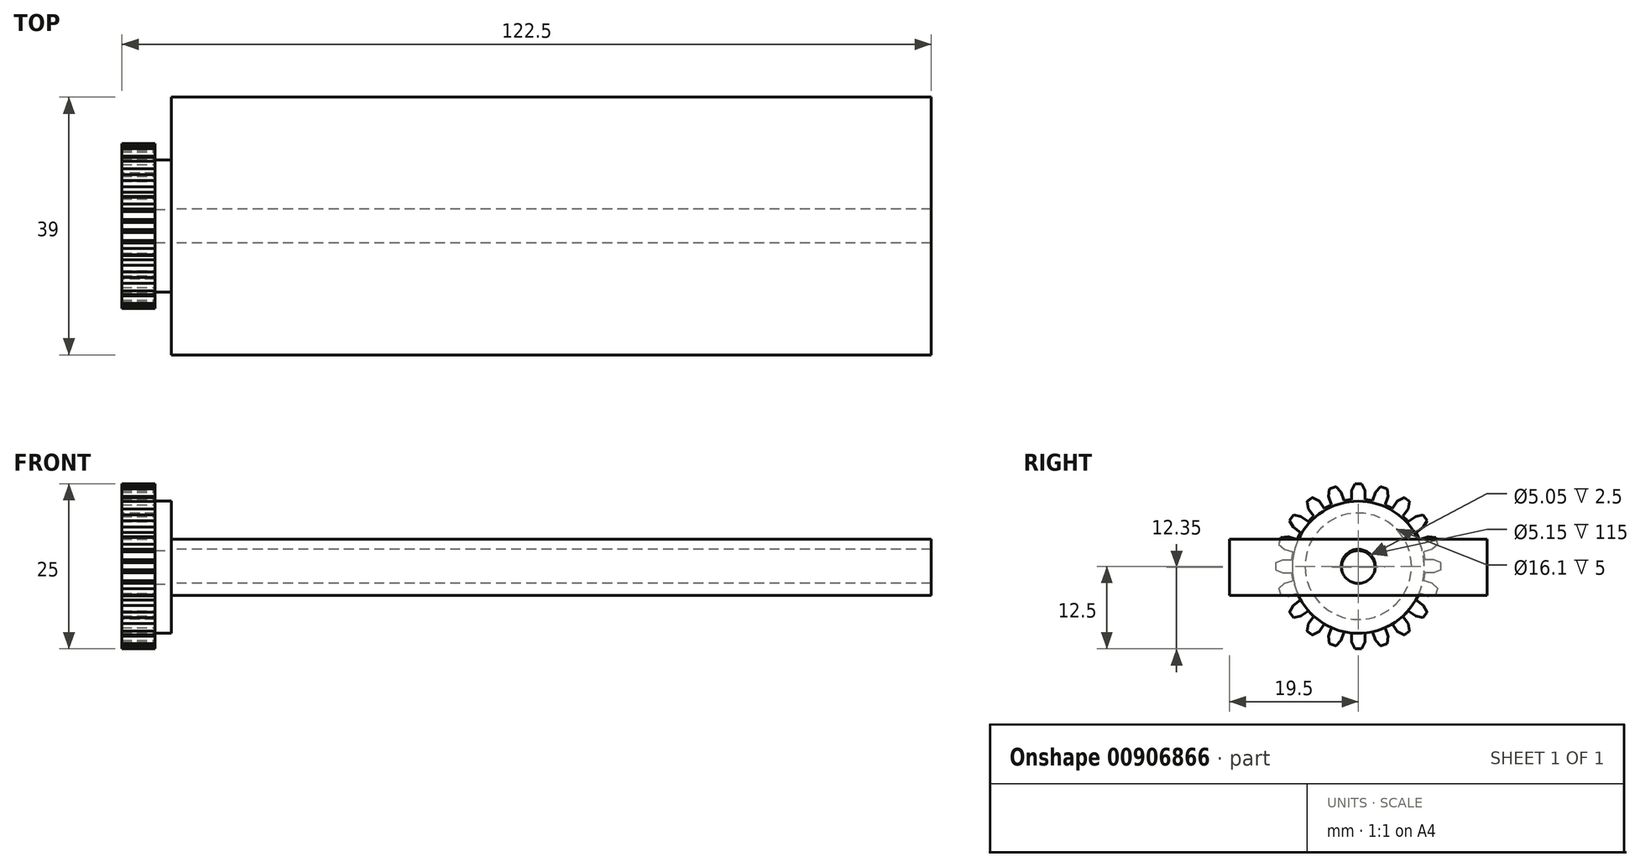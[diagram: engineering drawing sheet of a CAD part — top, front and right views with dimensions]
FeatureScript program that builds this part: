
annotation { "Feature Type Name" : "Feature", "Feature Type Description" : "" }
export const myFeature = defineFeature(function(context is Context, id is Id, definition is map)
    precondition{}
    {
        {
            var Q0;
            Q0=qCreatedBy(makeId("Top.planeOp"),FACE);
            var sketch = newSketch(context, id + "F0", { "sketchPlane" : qUnion([Q0])});
            skLineSegment(sketch, "E0.bottom", {"start": v(57.5, 19.5) * mm, "end": v(-57.5, 19.5) * mm});
            skLineSegment(sketch, "E0.top", {"start": v(57.5, -19.5) * mm, "end": v(-57.5, -19.5) * mm});
            skLineSegment(sketch, "E0.left", {"start": v(57.5, 19.5) * mm, "end": v(57.5, -19.5) * mm});
            skLineSegment(sketch, "E0.right", {"start": v(-57.5, 19.5) * mm, "end": v(-57.5, -19.5) * mm});
            skPoint(sketch, "E0.middle", {"position": v(0, 0) * mm});
            skSolve(sketch);
        }
        {
            var Q0;
            Q0 = qSketchRegion(id + "F0", true);
            extrude(context, id + "F1", {"entities" : qUnion([Q0]), "depth" : 8.5 * mm, "offsetDistance" : 25 * mm});
        }
        {
            var Q0;
            Q0=makeQuery(id+"F1.opExtrude","SWEPT_FACE",FACE,{"disambiguationData":[OSD([sQuery(id+"F0.wireOp",EDGE,"E0.right")])]});
            var sketch = newSketch(context, id + "F2", { "sketchPlane" : qUnion([Q0])});
            skLineSegment(sketch, "E1", {"start": v(-19.5, 4.25) * mm, "end": v(19.5, 4.25) * mm, "construction": true});
            skLineSegment(sketch, "E2", {"start": v(0, 8.5) * mm, "end": v(0, 0) * mm, "construction": true});
            skCircle(sketch, "E3", {"center": v(0, 4.25) * mm, "radius": 2.52 * mm});
            skCircle(sketch, "E4", {"center": v(0, 4.25) * mm, "radius": 10 * mm});
            skSolve(sketch);
        }
        {
            var Q0;
            Q0 = qSketchRegion(id + "F2", true);
            extrude(context, id + "F3", {"entities" : qUnion([Q0]), "operationType" : NewBodyOperationType.ADD, "depth" : 2.5 * mm, "offsetDistance" : 25 * mm});
        }
        {
            var Q0;
            {var subQ0=sQuery(id+"F0.wireOp",EDGE,"E0.right");var subQ1=makeQuery(id+"F1.opExtrude","SWEPT_FACE",FACE,{"disambiguationData":[OSD([subQ0])]});var subQ2=sQuery(id+"F0.wireOp",EDGE,"E0.top");Q0=makeQuery(id+"F3.boolean.opBoolean","SPLIT",FACE,{"disambiguationData":[TD([makeQuery(id+"F1.opExtrude","SWEPT_FACE",FACE,{"disambiguationData":[OSD([subQ2])]})])],"derivedFrom":subQ1});}
            var sketch = newSketch(context, id + "F4", { "sketchPlane" : qUnion([Q0])});
            skCircle(sketch, "E5.0", {"center": v(0, 4.4) * mm, "radius": 2.58 * mm});
            skSolve(sketch);
        }
        {
            var Q0;
            Q0 = qSketchRegion(id + "F4", true);
            extrude(context, id + "F5", {"entities" : qUnion([Q0]), "operationType" : NewBodyOperationType.REMOVE, "endBound" : BoundingType.THROUGH_ALL, "oppositeDirection" : true, "depth" : 90 * mm, "offsetDistance" : 25 * mm});
        }
        {
            var Q0;
            Q0=makeQuery(id+"F3.opExtrude","CAP_FACE",FACE,{"disambiguationData":[OSD([sQuery(id+"F2.wireOp",EDGE,"E3"),sQuery(id+"F2.wireOp",EDGE,"E4")])],"isStart":false});
            var sketch = newSketch(context, id + "F6", { "sketchPlane" : qUnion([Q0])});
            skCircle(sketch, "E6", {"center": v(0, 4.4) * mm, "radius": 11.5 * mm, "construction": true});
            skLineSegment(sketch, "E7", {"start": v(-0.52, 16.89) * mm, "end": v(-1, 15.86) * mm});
            skLineSegment(sketch, "E8", {"start": v(-1, 15.86) * mm, "end": v(-1, 14.5) * mm});
            skLineSegment(sketch, "E9", {"start": v(-0.52, 19.42) * mm, "end": v(-0.52, 14.1) * mm, "construction": true});
            skLineSegment(sketch, "E10.MirrorCS", {"start": v(0.52, 16.89) * mm, "end": v(1, 15.86) * mm});
            skLineSegment(sketch, "E11.MirrorCS", {"start": v(1, 15.86) * mm, "end": v(1, 14.5) * mm});
            skArc(sketch, "E12", {"start": v(-0.52, 16.89) * mm, "mid": v(0, 16.9) * mm, "end": v(0.52, 16.89) * mm});
            skLineSegment(sketch, "E13.1.0", {"start": v(-4.5, 14.99) * mm, "end": v(-4.07, 13.7) * mm});
            skLineSegment(sketch, "E13.1.1", {"start": v(-3.37, 16.44) * mm, "end": v(-2.59, 15.6) * mm});
            skLineSegment(sketch, "E13.1.2", {"start": v(-2.59, 15.6) * mm, "end": v(-2.17, 14.31) * mm});
            skLineSegment(sketch, "E13.1.3", {"start": v(-4.35, 16.12) * mm, "end": v(-4.5, 14.99) * mm});
            skArc(sketch, "E13.1.4", {"start": v(-4.35, 16.12) * mm, "mid": v(-3.86, 16.29) * mm, "end": v(-3.37, 16.44) * mm});
            skLineSegment(sketch, "E13.2.0", {"start": v(-7.54, 13.08) * mm, "end": v(-6.74, 11.98) * mm});
            skLineSegment(sketch, "E13.2.1", {"start": v(-6.92, 14.8) * mm, "end": v(-5.92, 14.26) * mm});
            skLineSegment(sketch, "E13.2.2", {"start": v(-5.92, 14.26) * mm, "end": v(-5.13, 13.16) * mm});
            skLineSegment(sketch, "E13.2.3", {"start": v(-7.76, 14.2) * mm, "end": v(-7.54, 13.08) * mm});
            skArc(sketch, "E13.2.4", {"start": v(-7.76, 14.2) * mm, "mid": v(-7.35, 14.51) * mm, "end": v(-6.92, 14.8) * mm});
            skLineSegment(sketch, "E13.3.0", {"start": v(-9.86, 10.32) * mm, "end": v(-8.76, 9.53) * mm});
            skLineSegment(sketch, "E13.3.1", {"start": v(-9.8, 12.16) * mm, "end": v(-8.68, 11.94) * mm});
            skLineSegment(sketch, "E13.3.2", {"start": v(-8.68, 11.94) * mm, "end": v(-7.58, 11.14) * mm});
            skLineSegment(sketch, "E13.3.3", {"start": v(-10.4, 11.32) * mm, "end": v(-9.86, 10.32) * mm});
            skArc(sketch, "E13.3.4", {"start": v(-10.4, 11.32) * mm, "mid": v(-10.11, 11.75) * mm, "end": v(-9.8, 12.16) * mm});
            skLineSegment(sketch, "E13.4.0", {"start": v(-11.2, 6.99) * mm, "end": v(-9.91, 6.57) * mm});
            skLineSegment(sketch, "E13.4.1", {"start": v(-11.72, 8.75) * mm, "end": v(-10.59, 8.9) * mm});
            skLineSegment(sketch, "E13.4.2", {"start": v(-10.59, 8.9) * mm, "end": v(-9.3, 8.47) * mm});
            skLineSegment(sketch, "E13.4.3", {"start": v(-12.04, 7.77) * mm, "end": v(-11.2, 6.99) * mm});
            skArc(sketch, "E13.4.4", {"start": v(-12.04, 7.77) * mm, "mid": v(-11.89, 8.26) * mm, "end": v(-11.72, 8.75) * mm});
            skLineSegment(sketch, "E13.5.0", {"start": v(-11.46, 3.4) * mm, "end": v(-10.1, 3.4) * mm});
            skLineSegment(sketch, "E13.5.1", {"start": v(-12.49, 4.92) * mm, "end": v(-11.46, 5.4) * mm});
            skLineSegment(sketch, "E13.5.2", {"start": v(-11.46, 5.4) * mm, "end": v(-10.1, 5.4) * mm});
            skLineSegment(sketch, "E13.5.3", {"start": v(-12.49, 3.88) * mm, "end": v(-11.46, 3.4) * mm});
            skArc(sketch, "E13.5.4", {"start": v(-12.49, 3.88) * mm, "mid": v(-12.5, 4.4) * mm, "end": v(-12.49, 4.92) * mm});
            skLineSegment(sketch, "E13.6.0", {"start": v(-10.59, -0.1) * mm, "end": v(-9.3, 0.33) * mm});
            skLineSegment(sketch, "E13.6.1", {"start": v(-12.04, 1.03) * mm, "end": v(-11.2, 1.81) * mm});
            skLineSegment(sketch, "E13.6.2", {"start": v(-11.2, 1.81) * mm, "end": v(-9.91, 2.23) * mm});
            skLineSegment(sketch, "E13.6.3", {"start": v(-11.72, 0.05) * mm, "end": v(-10.59, -0.1) * mm});
            skArc(sketch, "E13.6.4", {"start": v(-11.72, 0.05) * mm, "mid": v(-11.89, 0.54) * mm, "end": v(-12.04, 1.03) * mm});
            skLineSegment(sketch, "E13.7.0", {"start": v(-8.68, -3.14) * mm, "end": v(-7.58, -2.34) * mm});
            skLineSegment(sketch, "E13.7.1", {"start": v(-10.4, -2.52) * mm, "end": v(-9.86, -1.52) * mm});
            skLineSegment(sketch, "E13.7.2", {"start": v(-9.86, -1.52) * mm, "end": v(-8.76, -0.73) * mm});
            skLineSegment(sketch, "E13.7.3", {"start": v(-9.8, -3.36) * mm, "end": v(-8.68, -3.14) * mm});
            skArc(sketch, "E13.7.4", {"start": v(-9.8, -3.36) * mm, "mid": v(-10.11, -2.95) * mm, "end": v(-10.4, -2.52) * mm});
            skLineSegment(sketch, "E13.8.0", {"start": v(-5.92, -5.46) * mm, "end": v(-5.13, -4.36) * mm});
            skLineSegment(sketch, "E13.8.1", {"start": v(-7.76, -5.4) * mm, "end": v(-7.54, -4.28) * mm});
            skLineSegment(sketch, "E13.8.2", {"start": v(-7.54, -4.28) * mm, "end": v(-6.74, -3.18) * mm});
            skLineSegment(sketch, "E13.8.3", {"start": v(-6.92, -6) * mm, "end": v(-5.92, -5.46) * mm});
            skArc(sketch, "E13.8.4", {"start": v(-6.92, -6) * mm, "mid": v(-7.35, -5.71) * mm, "end": v(-7.76, -5.4) * mm});
            skLineSegment(sketch, "E13.9.0", {"start": v(-2.59, -6.8) * mm, "end": v(-2.17, -5.51) * mm});
            skLineSegment(sketch, "E13.9.1", {"start": v(-4.35, -7.32) * mm, "end": v(-4.5, -6.19) * mm});
            skLineSegment(sketch, "E13.9.2", {"start": v(-4.5, -6.19) * mm, "end": v(-4.07, -4.9) * mm});
            skLineSegment(sketch, "E13.9.3", {"start": v(-3.37, -7.64) * mm, "end": v(-2.59, -6.8) * mm});
            skArc(sketch, "E13.9.4", {"start": v(-3.37, -7.64) * mm, "mid": v(-3.86, -7.49) * mm, "end": v(-4.35, -7.32) * mm});
            skLineSegment(sketch, "E13.10.0", {"start": v(1, -7.06) * mm, "end": v(1, -5.7) * mm});
            skLineSegment(sketch, "E13.10.1", {"start": v(-0.52, -8.09) * mm, "end": v(-1, -7.06) * mm});
            skLineSegment(sketch, "E13.10.2", {"start": v(-1, -7.06) * mm, "end": v(-1, -5.7) * mm});
            skLineSegment(sketch, "E13.10.3", {"start": v(0.52, -8.09) * mm, "end": v(1, -7.06) * mm});
            skArc(sketch, "E13.10.4", {"start": v(0.52, -8.09) * mm, "mid": v(0, -8.1) * mm, "end": v(-0.52, -8.09) * mm});
            skLineSegment(sketch, "E13.11.0", {"start": v(4.5, -6.19) * mm, "end": v(4.07, -4.9) * mm});
            skLineSegment(sketch, "E13.11.1", {"start": v(3.37, -7.64) * mm, "end": v(2.59, -6.8) * mm});
            skLineSegment(sketch, "E13.11.2", {"start": v(2.59, -6.8) * mm, "end": v(2.17, -5.51) * mm});
            skLineSegment(sketch, "E13.11.3", {"start": v(4.35, -7.32) * mm, "end": v(4.5, -6.19) * mm});
            skArc(sketch, "E13.11.4", {"start": v(4.35, -7.32) * mm, "mid": v(3.86, -7.49) * mm, "end": v(3.37, -7.64) * mm});
            skLineSegment(sketch, "E13.12.0", {"start": v(7.54, -4.28) * mm, "end": v(6.74, -3.18) * mm});
            skLineSegment(sketch, "E13.12.1", {"start": v(6.92, -6) * mm, "end": v(5.92, -5.46) * mm});
            skLineSegment(sketch, "E13.12.2", {"start": v(5.92, -5.46) * mm, "end": v(5.13, -4.36) * mm});
            skLineSegment(sketch, "E13.12.3", {"start": v(7.76, -5.4) * mm, "end": v(7.54, -4.28) * mm});
            skArc(sketch, "E13.12.4", {"start": v(7.76, -5.4) * mm, "mid": v(7.35, -5.71) * mm, "end": v(6.92, -6) * mm});
            skLineSegment(sketch, "E13.13.0", {"start": v(9.86, -1.52) * mm, "end": v(8.76, -0.73) * mm});
            skLineSegment(sketch, "E13.13.1", {"start": v(9.8, -3.36) * mm, "end": v(8.68, -3.14) * mm});
            skLineSegment(sketch, "E13.13.2", {"start": v(8.68, -3.14) * mm, "end": v(7.58, -2.34) * mm});
            skLineSegment(sketch, "E13.13.3", {"start": v(10.4, -2.52) * mm, "end": v(9.86, -1.52) * mm});
            skArc(sketch, "E13.13.4", {"start": v(10.4, -2.52) * mm, "mid": v(10.11, -2.95) * mm, "end": v(9.8, -3.36) * mm});
            skLineSegment(sketch, "E13.14.0", {"start": v(11.2, 1.81) * mm, "end": v(9.91, 2.23) * mm});
            skLineSegment(sketch, "E13.14.1", {"start": v(11.72, 0.05) * mm, "end": v(10.59, -0.1) * mm});
            skLineSegment(sketch, "E13.14.2", {"start": v(10.59, -0.1) * mm, "end": v(9.3, 0.33) * mm});
            skLineSegment(sketch, "E13.14.3", {"start": v(12.04, 1.03) * mm, "end": v(11.2, 1.81) * mm});
            skArc(sketch, "E13.14.4", {"start": v(12.04, 1.03) * mm, "mid": v(11.89, 0.54) * mm, "end": v(11.72, 0.05) * mm});
            skLineSegment(sketch, "E13.15.0", {"start": v(11.46, 5.4) * mm, "end": v(10.1, 5.4) * mm});
            skLineSegment(sketch, "E13.15.1", {"start": v(12.49, 3.88) * mm, "end": v(11.46, 3.4) * mm});
            skLineSegment(sketch, "E13.15.2", {"start": v(11.46, 3.4) * mm, "end": v(10.1, 3.4) * mm});
            skLineSegment(sketch, "E13.15.3", {"start": v(12.49, 4.92) * mm, "end": v(11.46, 5.4) * mm});
            skArc(sketch, "E13.15.4", {"start": v(12.49, 4.92) * mm, "mid": v(12.5, 4.4) * mm, "end": v(12.49, 3.88) * mm});
            skLineSegment(sketch, "E13.16.0", {"start": v(10.59, 8.9) * mm, "end": v(9.3, 8.47) * mm});
            skLineSegment(sketch, "E13.16.1", {"start": v(12.04, 7.77) * mm, "end": v(11.2, 6.99) * mm});
            skLineSegment(sketch, "E13.16.2", {"start": v(11.2, 6.99) * mm, "end": v(9.91, 6.57) * mm});
            skLineSegment(sketch, "E13.16.3", {"start": v(11.72, 8.75) * mm, "end": v(10.59, 8.9) * mm});
            skArc(sketch, "E13.16.4", {"start": v(11.72, 8.75) * mm, "mid": v(11.89, 8.26) * mm, "end": v(12.04, 7.77) * mm});
            skLineSegment(sketch, "E13.17.0", {"start": v(8.68, 11.94) * mm, "end": v(7.58, 11.14) * mm});
            skLineSegment(sketch, "E13.17.1", {"start": v(10.4, 11.32) * mm, "end": v(9.86, 10.32) * mm});
            skLineSegment(sketch, "E13.17.2", {"start": v(9.86, 10.32) * mm, "end": v(8.76, 9.53) * mm});
            skLineSegment(sketch, "E13.17.3", {"start": v(9.8, 12.16) * mm, "end": v(8.68, 11.94) * mm});
            skArc(sketch, "E13.17.4", {"start": v(9.8, 12.16) * mm, "mid": v(10.11, 11.75) * mm, "end": v(10.4, 11.32) * mm});
            skLineSegment(sketch, "E13.18.0", {"start": v(5.92, 14.26) * mm, "end": v(5.13, 13.16) * mm});
            skLineSegment(sketch, "E13.18.1", {"start": v(7.76, 14.2) * mm, "end": v(7.54, 13.08) * mm});
            skLineSegment(sketch, "E13.18.2", {"start": v(7.54, 13.08) * mm, "end": v(6.74, 11.98) * mm});
            skLineSegment(sketch, "E13.18.3", {"start": v(6.92, 14.8) * mm, "end": v(5.92, 14.26) * mm});
            skArc(sketch, "E13.18.4", {"start": v(6.92, 14.8) * mm, "mid": v(7.35, 14.51) * mm, "end": v(7.76, 14.2) * mm});
            skLineSegment(sketch, "E13.19.0", {"start": v(2.59, 15.6) * mm, "end": v(2.17, 14.31) * mm});
            skLineSegment(sketch, "E13.19.1", {"start": v(4.35, 16.12) * mm, "end": v(4.5, 14.99) * mm});
            skLineSegment(sketch, "E13.19.2", {"start": v(4.5, 14.99) * mm, "end": v(4.07, 13.7) * mm});
            skLineSegment(sketch, "E13.19.3", {"start": v(3.37, 16.44) * mm, "end": v(2.59, 15.6) * mm});
            skArc(sketch, "E13.19.4", {"start": v(3.37, 16.44) * mm, "mid": v(3.86, 16.29) * mm, "end": v(4.35, 16.12) * mm});
            skArc(sketch, "E14", {"start": v(-4.07, 13.7) * mm, "mid": v(-4.6, 13.44) * mm, "end": v(-5.13, 13.16) * mm});
            skArc(sketch, "E15.trimOffspring", {"start": v(-6.74, 11.98) * mm, "mid": v(-7.17, 11.57) * mm, "end": v(-7.58, 11.14) * mm});
            skArc(sketch, "E16.trimOffspring", {"start": v(-8.76, 9.53) * mm, "mid": v(-9.04, 9) * mm, "end": v(-9.3, 8.47) * mm});
            skArc(sketch, "E17.trimOffspring", {"start": v(-9.91, 6.57) * mm, "mid": v(-10.02, 5.99) * mm, "end": v(-10.1, 5.4) * mm});
            skArc(sketch, "E18.trimOffspring", {"start": v(-10.1, 3.4) * mm, "mid": v(-10.02, 2.81) * mm, "end": v(-9.91, 2.23) * mm});
            skArc(sketch, "E19.trimOffspring", {"start": v(-9.3, 0.33) * mm, "mid": v(-9.04, -0.2) * mm, "end": v(-8.76, -0.73) * mm});
            skArc(sketch, "E20.trimOffspring", {"start": v(-7.58, -2.34) * mm, "mid": v(-7.17, -2.77) * mm, "end": v(-6.74, -3.18) * mm});
            skArc(sketch, "E21.trimOffspring", {"start": v(-5.13, -4.36) * mm, "mid": v(-4.6, -4.64) * mm, "end": v(-4.07, -4.9) * mm});
            skArc(sketch, "E22.trimOffspring", {"start": v(-2.17, -5.51) * mm, "mid": v(-1.59, -5.62) * mm, "end": v(-1, -5.7) * mm});
            skArc(sketch, "E23.trimOffspring", {"start": v(1, -5.7) * mm, "mid": v(1.59, -5.62) * mm, "end": v(2.17, -5.51) * mm});
            skArc(sketch, "E24.trimOffspring", {"start": v(4.07, -4.9) * mm, "mid": v(4.6, -4.64) * mm, "end": v(5.13, -4.36) * mm});
            skArc(sketch, "E25.trimOffspring", {"start": v(6.74, -3.18) * mm, "mid": v(7.17, -2.77) * mm, "end": v(7.58, -2.34) * mm});
            skArc(sketch, "E26.trimOffspring", {"start": v(8.76, -0.73) * mm, "mid": v(9.04, -0.2) * mm, "end": v(9.3, 0.33) * mm});
            skArc(sketch, "E27.trimOffspring", {"start": v(9.91, 2.23) * mm, "mid": v(10.02, 2.81) * mm, "end": v(10.1, 3.4) * mm});
            skArc(sketch, "E28.trimOffspring", {"start": v(10.1, 5.4) * mm, "mid": v(10.02, 5.99) * mm, "end": v(9.91, 6.57) * mm});
            skArc(sketch, "E29.trimOffspring", {"start": v(9.3, 8.47) * mm, "mid": v(9.04, 9) * mm, "end": v(8.76, 9.53) * mm});
            skArc(sketch, "E30.trimOffspring", {"start": v(7.58, 11.14) * mm, "mid": v(7.17, 11.57) * mm, "end": v(6.74, 11.98) * mm});
            skArc(sketch, "E31.trimOffspring", {"start": v(5.13, 13.16) * mm, "mid": v(4.6, 13.44) * mm, "end": v(4.07, 13.7) * mm});
            skArc(sketch, "E32.trimOffspring", {"start": v(2.17, 14.31) * mm, "mid": v(1.59, 14.42) * mm, "end": v(1, 14.5) * mm});
            skArc(sketch, "E33.trimOffspring", {"start": v(-0.52, 14.53) * mm, "mid": v(-1.35, 14.46) * mm, "end": v(-2.17, 14.31) * mm});
            skLineSegment(sketch, "E34", {"start": v(-19.5, 4.4) * mm, "end": v(19.5, 4.4) * mm, "construction": true});
            skSolve(sketch);
        }
        {
            var Q0;
            Q0 = qSketchRegion(id + "F6", true);
            extrude(context, id + "F7", {"entities" : qUnion([Q0]), "operationType" : NewBodyOperationType.ADD, "depth" : 5 * mm, "offsetDistance" : 25 * mm});
        }
        {
            var Q0;
            Q0=makeQuery(id+"F7.opExtrude","CAP_FACE",FACE,{"disambiguationData":[OSD([sQuery(id+"F6.wireOp",EDGE,"E7"),sQuery(id+"F6.wireOp",EDGE,"E8"),sQuery(id+"F6.wireOp",EDGE,"E10.MirrorCS"),sQuery(id+"F6.wireOp",EDGE,"E11.MirrorCS"),sQuery(id+"F6.wireOp",EDGE,"E12"),sQuery(id+"F6.wireOp",EDGE,"E13.1.0"),sQuery(id+"F6.wireOp",EDGE,"E13.1.1"),sQuery(id+"F6.wireOp",EDGE,"E13.1.2"),sQuery(id+"F6.wireOp",EDGE,"E13.1.3"),sQuery(id+"F6.wireOp",EDGE,"E13.1.4"),sQuery(id+"F6.wireOp",EDGE,"E13.2.0"),sQuery(id+"F6.wireOp",EDGE,"E13.2.1"),sQuery(id+"F6.wireOp",EDGE,"E13.2.2"),sQuery(id+"F6.wireOp",EDGE,"E13.2.3"),sQuery(id+"F6.wireOp",EDGE,"E13.2.4"),sQuery(id+"F6.wireOp",EDGE,"E13.3.0"),sQuery(id+"F6.wireOp",EDGE,"E13.3.1"),sQuery(id+"F6.wireOp",EDGE,"E13.3.2"),sQuery(id+"F6.wireOp",EDGE,"E13.3.3"),sQuery(id+"F6.wireOp",EDGE,"E13.3.4"),sQuery(id+"F6.wireOp",EDGE,"E13.4.0"),sQuery(id+"F6.wireOp",EDGE,"E13.4.1"),sQuery(id+"F6.wireOp",EDGE,"E13.4.2"),sQuery(id+"F6.wireOp",EDGE,"E13.4.3"),sQuery(id+"F6.wireOp",EDGE,"E13.4.4"),sQuery(id+"F6.wireOp",EDGE,"E13.5.0"),sQuery(id+"F6.wireOp",EDGE,"E13.5.1"),sQuery(id+"F6.wireOp",EDGE,"E13.5.2"),sQuery(id+"F6.wireOp",EDGE,"E13.5.3"),sQuery(id+"F6.wireOp",EDGE,"E13.5.4"),sQuery(id+"F6.wireOp",EDGE,"E13.6.0"),sQuery(id+"F6.wireOp",EDGE,"E13.6.1"),sQuery(id+"F6.wireOp",EDGE,"E13.6.2"),sQuery(id+"F6.wireOp",EDGE,"E13.6.3"),sQuery(id+"F6.wireOp",EDGE,"E13.6.4"),sQuery(id+"F6.wireOp",EDGE,"E13.7.0"),sQuery(id+"F6.wireOp",EDGE,"E13.7.1"),sQuery(id+"F6.wireOp",EDGE,"E13.7.2"),sQuery(id+"F6.wireOp",EDGE,"E13.7.3"),sQuery(id+"F6.wireOp",EDGE,"E13.7.4"),sQuery(id+"F6.wireOp",EDGE,"E13.8.0"),sQuery(id+"F6.wireOp",EDGE,"E13.8.1"),sQuery(id+"F6.wireOp",EDGE,"E13.8.2"),sQuery(id+"F6.wireOp",EDGE,"E13.8.3"),sQuery(id+"F6.wireOp",EDGE,"E13.8.4"),sQuery(id+"F6.wireOp",EDGE,"E13.9.0"),sQuery(id+"F6.wireOp",EDGE,"E13.9.1"),sQuery(id+"F6.wireOp",EDGE,"E13.9.2"),sQuery(id+"F6.wireOp",EDGE,"E13.9.3"),sQuery(id+"F6.wireOp",EDGE,"E13.9.4"),sQuery(id+"F6.wireOp",EDGE,"E13.10.0"),sQuery(id+"F6.wireOp",EDGE,"E13.10.1"),sQuery(id+"F6.wireOp",EDGE,"E13.10.2"),sQuery(id+"F6.wireOp",EDGE,"E13.10.3"),sQuery(id+"F6.wireOp",EDGE,"E13.10.4"),sQuery(id+"F6.wireOp",EDGE,"E13.11.0"),sQuery(id+"F6.wireOp",EDGE,"E13.11.1"),sQuery(id+"F6.wireOp",EDGE,"E13.11.2"),sQuery(id+"F6.wireOp",EDGE,"E13.11.3"),sQuery(id+"F6.wireOp",EDGE,"E13.11.4"),sQuery(id+"F6.wireOp",EDGE,"E13.12.0"),sQuery(id+"F6.wireOp",EDGE,"E13.12.1"),sQuery(id+"F6.wireOp",EDGE,"E13.12.2"),sQuery(id+"F6.wireOp",EDGE,"E13.12.3"),sQuery(id+"F6.wireOp",EDGE,"E13.12.4"),sQuery(id+"F6.wireOp",EDGE,"E13.13.0"),sQuery(id+"F6.wireOp",EDGE,"E13.13.1"),sQuery(id+"F6.wireOp",EDGE,"E13.13.2"),sQuery(id+"F6.wireOp",EDGE,"E13.13.3"),sQuery(id+"F6.wireOp",EDGE,"E13.13.4"),sQuery(id+"F6.wireOp",EDGE,"E13.14.0"),sQuery(id+"F6.wireOp",EDGE,"E13.14.1"),sQuery(id+"F6.wireOp",EDGE,"E13.14.2"),sQuery(id+"F6.wireOp",EDGE,"E13.14.3"),sQuery(id+"F6.wireOp",EDGE,"E13.14.4"),sQuery(id+"F6.wireOp",EDGE,"E13.15.0"),sQuery(id+"F6.wireOp",EDGE,"E13.15.1"),sQuery(id+"F6.wireOp",EDGE,"E13.15.2"),sQuery(id+"F6.wireOp",EDGE,"E13.15.3"),sQuery(id+"F6.wireOp",EDGE,"E13.15.4"),sQuery(id+"F6.wireOp",EDGE,"E13.16.0"),sQuery(id+"F6.wireOp",EDGE,"E13.16.1"),sQuery(id+"F6.wireOp",EDGE,"E13.16.2"),sQuery(id+"F6.wireOp",EDGE,"E13.16.3"),sQuery(id+"F6.wireOp",EDGE,"E13.16.4"),sQuery(id+"F6.wireOp",EDGE,"E13.17.0"),sQuery(id+"F6.wireOp",EDGE,"E13.17.1"),sQuery(id+"F6.wireOp",EDGE,"E13.17.2"),sQuery(id+"F6.wireOp",EDGE,"E13.17.3"),sQuery(id+"F6.wireOp",EDGE,"E13.17.4"),sQuery(id+"F6.wireOp",EDGE,"E13.18.0"),sQuery(id+"F6.wireOp",EDGE,"E13.18.1"),sQuery(id+"F6.wireOp",EDGE,"E13.18.2"),sQuery(id+"F6.wireOp",EDGE,"E13.18.3"),sQuery(id+"F6.wireOp",EDGE,"E13.18.4"),sQuery(id+"F6.wireOp",EDGE,"E13.19.0"),sQuery(id+"F6.wireOp",EDGE,"E13.19.1"),sQuery(id+"F6.wireOp",EDGE,"E13.19.2"),sQuery(id+"F6.wireOp",EDGE,"E13.19.3"),sQuery(id+"F6.wireOp",EDGE,"E13.19.4"),sQuery(id+"F6.wireOp",EDGE,"E14"),sQuery(id+"F6.wireOp",EDGE,"E15.trimOffspring"),sQuery(id+"F6.wireOp",EDGE,"E16.trimOffspring"),sQuery(id+"F6.wireOp",EDGE,"E17.trimOffspring"),sQuery(id+"F6.wireOp",EDGE,"E18.trimOffspring"),sQuery(id+"F6.wireOp",EDGE,"E19.trimOffspring"),sQuery(id+"F6.wireOp",EDGE,"E20.trimOffspring"),sQuery(id+"F6.wireOp",EDGE,"E21.trimOffspring"),sQuery(id+"F6.wireOp",EDGE,"E22.trimOffspring"),sQuery(id+"F6.wireOp",EDGE,"E23.trimOffspring"),sQuery(id+"F6.wireOp",EDGE,"E24.trimOffspring"),sQuery(id+"F6.wireOp",EDGE,"E25.trimOffspring"),sQuery(id+"F6.wireOp",EDGE,"E26.trimOffspring"),sQuery(id+"F6.wireOp",EDGE,"E27.trimOffspring"),sQuery(id+"F6.wireOp",EDGE,"E28.trimOffspring"),sQuery(id+"F6.wireOp",EDGE,"E29.trimOffspring"),sQuery(id+"F6.wireOp",EDGE,"E30.trimOffspring"),sQuery(id+"F6.wireOp",EDGE,"E31.trimOffspring"),sQuery(id+"F6.wireOp",EDGE,"E32.trimOffspring"),sQuery(id+"F6.wireOp",EDGE,"E33.trimOffspring")])],"isStart":false});
            var sketch = newSketch(context, id + "F8", { "sketchPlane" : qUnion([Q0])});
            skCircle(sketch, "E35", {"center": v(0, 4.4) * mm, "radius": 8.05 * mm});
            skSolve(sketch);
        }
        {
            var Q0;
            Q0 = qSketchRegion(id + "F8", true);
            extrude(context, id + "F9", {"entities" : qUnion([Q0]), "operationType" : NewBodyOperationType.REMOVE, "oppositeDirection" : true, "depth" : 5 * mm, "offsetDistance" : 25 * mm});
        }
    });
